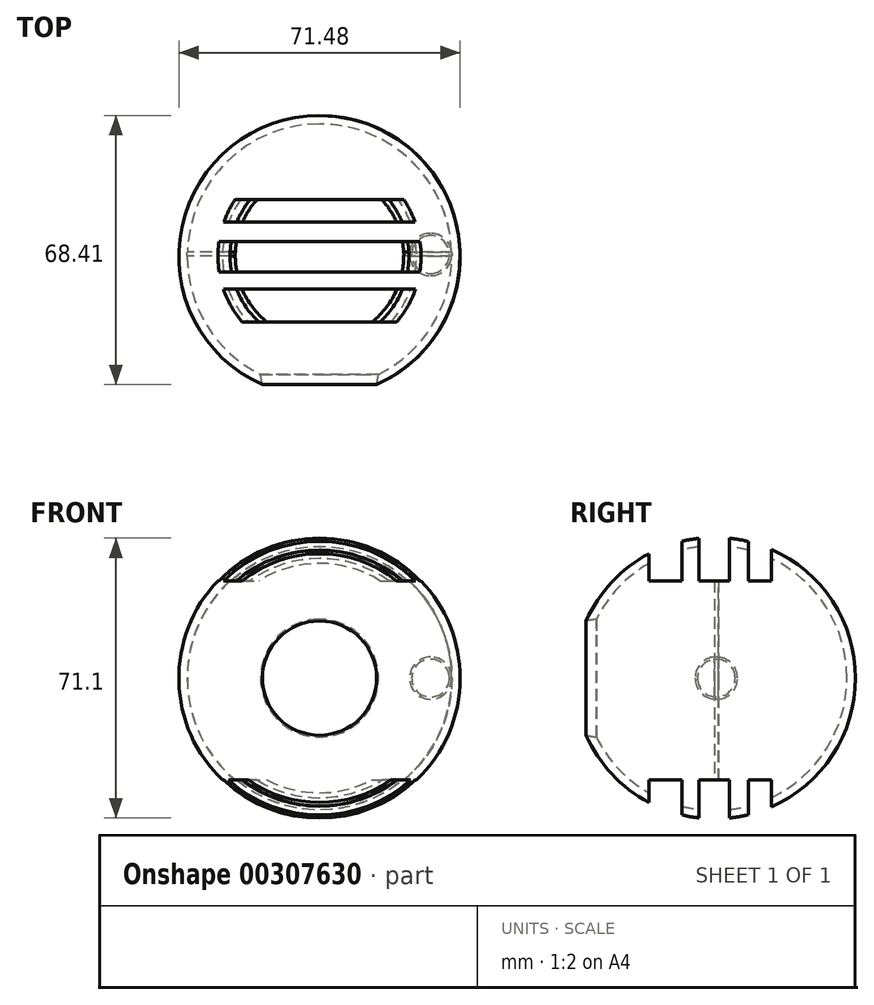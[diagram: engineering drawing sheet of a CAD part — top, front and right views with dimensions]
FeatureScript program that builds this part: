
annotation { "Feature Type Name" : "Feature", "Feature Type Description" : "" }
export const myFeature = defineFeature(function(context is Context, id is Id, definition is map)
    precondition{}
    {
        {
            var Q0;
            Q0=qCreatedBy(makeId("Top.planeOp"),FACE);
            var sketch = newSketch(context, id + "F0", { "sketchPlane" : qUnion([Q0])});
            skArc(sketch, "E0", {"start": v(14.5, 6.19) * mm, "mid": v(34.97, 46.27) * mm, "end": v(0, 74.6) * mm});
            skArc(sketch, "E1", {"start": v(0, 5.26) * mm, "mid": v(33.6, 38.85) * mm, "end": v(0, 72.45) * mm});
            skLineSegment(sketch, "E2", {"start": v(0, 74.6) * mm, "end": v(0, 72.45) * mm, "construction": true});
            skLineSegment(sketch, "E3", {"start": v(0, 3.1) * mm, "end": v(0, 5.26) * mm, "construction": true});
            skLineSegment(sketch, "E4", {"start": v(0, 74.6) * mm, "end": v(0, 72.45) * mm});
            skLineSegment(sketch, "E5", {"start": v(0, 0) * mm, "end": v(0, -64.47) * mm, "construction": true});
            skLineSegment(sketch, "E6", {"start": v(0, -64.47) * mm, "end": v(14.97, -64.47) * mm, "construction": true});
            skLineSegment(sketch, "E7", {"start": v(14.97, -64.47) * mm, "end": v(14.97, 6.4) * mm, "construction": true});
            skFitSpline(sketch, "E8", {"points": [v(14.97, 8.78) * mm, v(8.63, -10.94) * mm, v(6.04, -29.36) * mm, v(9.79, -46.05) * mm, v(0, -64.47) * mm], "startDerivative": vector(-13.39, -91.44) * mm, "endDerivative": vector(-68.18, -44.81) * mm});
            skLineSegment(sketch, "E9", {"start": v(0, -64.47) * mm, "end": v(0, 0) * mm});
            skLineSegment(sketch, "E10.trimOffspring", {"start": v(0, 72.45) * mm, "end": v(0, 74.6) * mm, "construction": true});
            skLineSegment(sketch, "E11.trimOffspring", {"start": v(0, 5.26) * mm, "end": v(0, 3.1) * mm, "construction": true});
            skLineSegment(sketch, "E12.trimOffspring", {"start": v(0, 5.26) * mm, "end": v(0, -76.27) * mm});
            skArc(sketch, "E13", {"start": v(28.22, 33.88) * mm, "mid": v(33.61, 39.27) * mm, "end": v(28.22, 44.66) * mm});
            skPoint(sketch, "E13.first.point", {"position": v(33.6, 38.85) * mm});
            skPoint(sketch, "E13.second.point", {"position": v(22.85, 38.85) * mm});
            skPoint(sketch, "E13.second.point.positionSnap0", {"position": v(33.6, 38.85) * mm});
            skPoint(sketch, "E13.third.point", {"position": v(24, 35.93) * mm});
            skArc(sketch, "E14", {"start": v(28.22, 34.47) * mm, "mid": v(33.03, 39.27) * mm, "end": v(28.22, 44.07) * mm});
            skLineSegment(sketch, "E15", {"start": v(28.22, 44.07) * mm, "end": v(28.22, 44.66) * mm});
            skLineSegment(sketch, "E16", {"start": v(28.22, 44.66) * mm, "end": v(28.22, 44.07) * mm});
            skLineSegment(sketch, "E17.trimOffspring", {"start": v(28.22, 39.27) * mm, "end": v(28.22, 33.88) * mm});
            skSolve(sketch);
        }
        {
            var Q0;
            Q0=makeQuery(id+"F0.imprint","IMPRINT",FACE,{"disambiguationData":[TD([[makeQuery(id+"F0.imprint","IMPRINT",EDGE,{"derivedFrom":sQuery(id+"F0.wireOp",EDGE,"E0")}),1.0]])]});
            var Q1;
            Q1=sQuery(id+"F0.wireOp",EDGE,"E12.trimOffspring");
            revolve(context, id + "F1", {"entities" : qUnion([Q0]), "axis" : qUnion([Q1]), "revolveType" : RevolveType.FULL});
        }
        {
            var Q0;
            Q0=qCreatedBy(makeId("Right.planeOp"),FACE);
            var sketch = newSketch(context, id + "F2", { "sketchPlane" : qUnion([Q0])});
            skLineSegment(sketch, "E18.bottom", {"start": v(22.13, 53.24) * mm, "end": v(30.47, 53.24) * mm});
            skLineSegment(sketch, "E18.top", {"start": v(22.13, -60.15) * mm, "end": v(30.47, -60.15) * mm});
            skLineSegment(sketch, "E18.left", {"start": v(22.13, 53.24) * mm, "end": v(22.13, 24.75) * mm});
            skLineSegment(sketch, "E18.right", {"start": v(30.47, 53.24) * mm, "end": v(30.47, 24.75) * mm});
            skLineSegment(sketch, "E19.bottom", {"start": v(34.8, 52.38) * mm, "end": v(42.56, 52.38) * mm});
            skLineSegment(sketch, "E19.top", {"start": v(34.8, -54.1) * mm, "end": v(42.56, -54.1) * mm});
            skLineSegment(sketch, "E19.left", {"start": v(34.8, 52.38) * mm, "end": v(34.8, 24.75) * mm});
            skLineSegment(sketch, "E19.right", {"start": v(42.56, 52.38) * mm, "end": v(42.56, 24.75) * mm});
            skLineSegment(sketch, "E20.bottom", {"start": v(53.2, 52.67) * mm, "end": v(47.45, 52.67) * mm});
            skLineSegment(sketch, "E20.top", {"start": v(53.2, -59) * mm, "end": v(47.45, -59) * mm});
            skLineSegment(sketch, "E20.left", {"start": v(53.2, 52.67) * mm, "end": v(53.2, 24.75) * mm});
            skLineSegment(sketch, "E20.right", {"start": v(47.45, 52.67) * mm, "end": v(47.45, 24.75) * mm});
            skLineSegment(sketch, "E21.bottom", {"start": v(53.2, 24.75) * mm, "end": v(47.45, 24.75) * mm});
            skLineSegment(sketch, "E21.top", {"start": v(53.2, -25.9) * mm, "end": v(47.45, -25.9) * mm});
            skLineSegment(sketch, "E22.trimOffspring", {"start": v(53.2, -25.9) * mm, "end": v(53.2, -59) * mm});
            skLineSegment(sketch, "E23.trimOffspring", {"start": v(47.45, -25.9) * mm, "end": v(47.45, -59) * mm});
            skLineSegment(sketch, "E24.trimOffspring", {"start": v(42.56, -25.9) * mm, "end": v(42.56, -54.1) * mm});
            skLineSegment(sketch, "E25.trimOffspring", {"start": v(34.8, -25.9) * mm, "end": v(34.8, -54.1) * mm});
            skLineSegment(sketch, "E26.trimOffspring", {"start": v(22.13, -25.9) * mm, "end": v(22.13, -60.15) * mm});
            skLineSegment(sketch, "E27.trimOffspring", {"start": v(30.47, -25.9) * mm, "end": v(30.47, -60.15) * mm});
            skLineSegment(sketch, "E28.trimOffspring", {"start": v(30.47, -25.9) * mm, "end": v(22.13, -25.9) * mm});
            skLineSegment(sketch, "E29.trimOffspring", {"start": v(42.56, -25.9) * mm, "end": v(34.8, -25.9) * mm});
            skLineSegment(sketch, "E30.trimOffspring", {"start": v(42.56, 24.75) * mm, "end": v(34.8, 24.75) * mm});
            skLineSegment(sketch, "E31.trimOffspring", {"start": v(30.47, 24.75) * mm, "end": v(22.13, 24.75) * mm});
            skSolve(sketch);
        }
        {
            var Q0;
            Q0 = qSketchRegion(id + "F2", true);
            extrude(context, id + "F3", {"entities" : qUnion([Q0]), "operationType" : NewBodyOperationType.REMOVE, "endBound" : BoundingType.SYMMETRIC, "oppositeDirection" : true, "depth" : 120 * mm});
        }
        {
            var Q0;
            {var subQ0=sQuery(id+"F0.wireOp",EDGE,"E14");Q0=makeQuery(id+"F0.imprint","IMPRINT",FACE,{"disambiguationData":[TD([[makeQuery(id+"F0.imprint","IMPRINT",EDGE,{"derivedFrom":subQ0}),-1.0]])]});}
            var Q1;
            Q1=sQuery(id+"F0.wireOp",EDGE,"E17.trimOffspring");
            revolve(context, id + "F4", {"entities" : qUnion([Q0]), "axis" : qUnion([Q1]), "revolveType" : RevolveType.FULL});
        }
        {
            var Q0;
            Q0=qCreatedBy(makeId("Top.planeOp"),FACE);
            var sketch = newSketch(context, id + "F5", { "sketchPlane" : qUnion([Q0])});
            skCircle(sketch, "E32", {"center": v(0, -54.39) * mm, "radius": 3.5 * mm});
            skSolve(sketch);
        }
        {
            var Q0;
            Q0 = qSketchRegion(id + "F5", true);
            extrude(context, id + "F6", {"entities" : qUnion([Q0]), "operationType" : NewBodyOperationType.REMOVE, "endBound" : BoundingType.SYMMETRIC, "oppositeDirection" : true, "depth" : 25 * mm});
        }
    });
